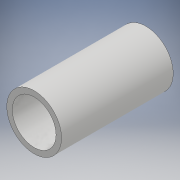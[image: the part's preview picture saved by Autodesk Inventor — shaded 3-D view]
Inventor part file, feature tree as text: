
AUTODESK INVENTOR PART (.ipt)
format: ipt  version: 2018.2 (Build 222227000, 227)  size: 97,280 bytes
history: native  units: mm
features: other x1, extrude x1, sketch x1
ambient origin geometry x8: Origin, YZ Plane, XZ Plane, XY Plane, X Axis, Y Axis, Z Axis, Center Point
bodies: Body1 (feature_tree)
feature tree (3):
  other  "ソリッド1"
  extrude  "押し出し1"  Depth=10.0mm
  sketch  "スケッチ1"
